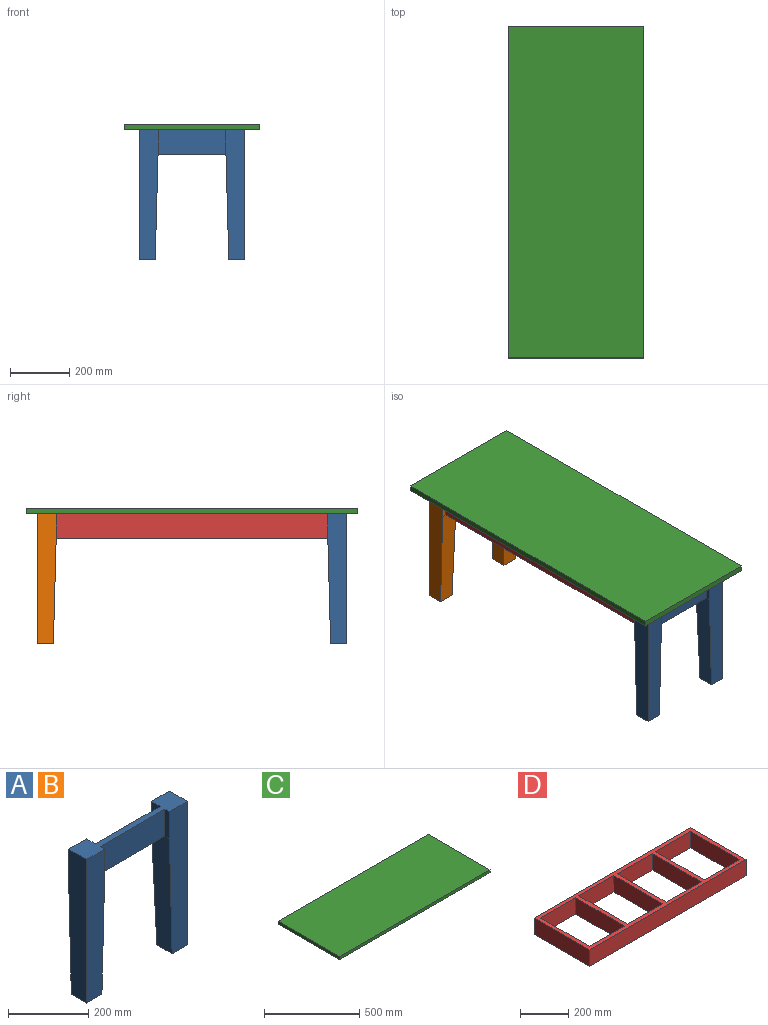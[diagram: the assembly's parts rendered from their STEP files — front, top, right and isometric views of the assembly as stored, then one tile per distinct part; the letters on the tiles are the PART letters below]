
ASSEMBLY  parts=4 mates=3
PART A: 20 faces, bbox 355.6x63.5x438.2 mm
  f0: plane 53.98x53.98mm, normal (0,0,-1), area 2913.3mm2, adj f1,f4,f5,f11
  f1: plane 438.15x63.5mm, normal (0,-1,0), area 26129mm2, adj f0,f3,f5,f6,f11
  f2: plane 82.55x30.93mm, normal (1,0,0), area 2553.6mm2, adj f6,f7,f8,f11
  f3: plane 82.55x15.88mm, normal (1,0,0), area 1310.5mm2, adj f1,f6,f9,f11
  f4: plane 355.6x63.5mm, normal (0,1,-0.03), area 20894.5mm2, adj f0,f5,f7,f11
  f5: plane 438.15x63.5mm, normal (-1,0,0), area 26129mm2, adj f0,f1,f4,f6,f7
  f6: plane 355.6x63.5mm, normal (0,0,1), area 11880mm2, adj f1,f2,f3,f5,f7,f8,f9,f13
  f7: plane 82.55x63.5mm, normal (0,1,0), area 5241.9mm2, adj f2,f4,f5,f6
  f8: plane 228.6x82.55mm, normal (0,1,0), area 18870.9mm2, adj f2,f6,f10,f14
  f9: plane 228.6x82.55mm, normal (0,-1,0), area 18870.9mm2, adj f3,f6,f10,f15
  f10: plane 228.6x16.69mm, normal (0,0,-1), area 3815.5mm2, adj f8,f9,f11,f19
  f11: plane 355.6x63.5mm, normal (1,0,-0.03), area 20894.5mm2, adj f0,f1,f2,f3,f4,f10
  f12: plane 53.98x53.98mm, normal (0,0,-1), area 2913.3mm2, adj f13,f16,f17,f19
  f13: plane 438.15x63.5mm, normal (0,-1,0), area 26129mm2, adj f6,f12,f15,f17,f19
  f14: plane 82.55x30.93mm, normal (-1,0,0), area 2553.6mm2, adj f6,f8,f18,f19
  f15: plane 82.55x15.88mm, normal (-1,0,0), area 1310.5mm2, adj f6,f9,f13,f19
  f16: plane 355.6x63.5mm, normal (0,1,-0.03), area 20894.5mm2, adj f12,f17,f18,f19
  f17: plane 438.15x63.5mm, normal (1,0,0), area 26129mm2, adj f6,f12,f13,f16,f18
  f18: plane 82.55x63.5mm, normal (0,1,0), area 5241.9mm2, adj f6,f14,f16,f17
  f19: plane 355.6x63.5mm, normal (-1,0,-0.03), area 20894.5mm2, adj f10,f12,f13,f14,f15,f16
PART B: same geometry as A
PART C: 6 faces, bbox 1117.6x457.2x19.1 mm
  f0: plane 457.2x19.05mm, normal (1,0,0), area 8709.7mm2, adj f1,f3,f4,f5
  f1: plane 1117.6x19.05mm, normal (0,1,0), area 21290.3mm2, adj f0,f2,f4,f5
  f2: plane 457.2x19.05mm, normal (-1,0,0), area 8709.7mm2, adj f1,f3,f4,f5
  f3: plane 1117.6x19.05mm, normal (0,-1,0), area 21290.3mm2, adj f0,f2,f4,f5
  f4: plane 1117.6x457.2mm, normal (0,0,1), area 510966.7mm2, adj f0,f1,f2,f3
  f5: plane 1117.6x457.2mm, normal (0,0,-1), area 510966.7mm2, adj f0,f1,f2,f3
PART D: 22 faces, bbox 914.4x323.9x82.6 mm
  f0: plane 204.79x82.55mm, normal (0,-1,0), area 16905.2mm2, adj f6,f7,f13,f21
  f1: plane 204.79x82.55mm, normal (0,1,0), area 16905.2mm2, adj f6,f7,f13,f21
  f2: plane 204.79x82.55mm, normal (0,-1,0), area 16905.2mm2, adj f6,f7,f16,f19
  f3: plane 204.79x82.55mm, normal (0,1,0), area 16905.2mm2, adj f6,f7,f16,f19
  f4: plane 204.79x82.55mm, normal (0,-1,0), area 16905.2mm2, adj f6,f7,f17,f20
  f5: plane 204.79x82.55mm, normal (0,1,0), area 16905.2mm2, adj f6,f7,f17,f20
  f6: plane 914.4x323.85mm, normal (0,0,1), area 62056.3mm2, adj f0,f1,f2,f3,f4,f5,f8,f9
  f7: plane 914.4x323.85mm, normal (0,0,-1), area 62056.3mm2, adj f0,f1,f2,f3,f4,f5,f8,f9
  f8: plane 323.85x82.55mm, normal (1,0,0), area 26733.8mm2, adj f6,f7,f9,f11
  f9: plane 914.4x82.55mm, normal (0,1,0), area 75483.7mm2, adj f6,f7,f8,f10
  f10: plane 323.85x82.55mm, normal (-1,0,0), area 26733.8mm2, adj f6,f7,f9,f11
  f11: plane 914.4x82.55mm, normal (0,-1,0), area 75483.7mm2, adj f6,f7,f8,f10
  f12: plane 204.79x82.55mm, normal (0,-1,0), area 16905.2mm2, adj f6,f7,f15,f18
  f13: plane 285.75x82.55mm, normal (-1,0,0), area 23588.7mm2, adj f0,f1,f6,f7
  f14: plane 204.79x82.55mm, normal (0,1,0), area 16905.2mm2, adj f6,f7,f15,f18
  f15: plane 285.75x82.55mm, normal (1,0,0), area 23588.7mm2, adj f6,f7,f12,f14
  f16: plane 285.75x82.55mm, normal (-1,0,0), area 23588.7mm2, adj f2,f3,f6,f7
  f17: plane 285.75x82.55mm, normal (1,0,0), area 23588.7mm2, adj f4,f5,f6,f7
  f18: plane 285.75x82.55mm, normal (-1,0,0), area 23588.7mm2, adj f6,f7,f12,f14
  f19: plane 285.75x82.55mm, normal (1,0,0), area 23588.7mm2, adj f2,f3,f6,f7
  f20: plane 285.75x82.55mm, normal (-1,0,0), area 23588.7mm2, adj f4,f5,f6,f7
  f21: plane 285.75x82.55mm, normal (1,0,0), area 23588.7mm2, adj f0,f1,f6,f7
PLACE A t=(-273.87,-633.92,65.37)mm
PLACE B rot(axis=(0,0,1),180deg) t=(18.23,280.49,65.37)mm
PLACE C rot(axis=(0,0,1),90deg) t=(-127.82,-185.61,284.45)mm
PLACE D rot(axis=(0,0,1),90deg) t=(-127.82,-176.72,201.9)mm
MATE parallel C.f5 <-> D.f6  axis (0,0,-1) through (-127.82,-176.72,284.45)mm
MATE parallel B.f8 <-> D.f8  axis (0,-1,0) through (-127.82,311.42,243.17)mm
MATE parallel D.f10 <-> A.f8  axis (0,-1,0) through (-127.82,-633.92,243.17)mm
